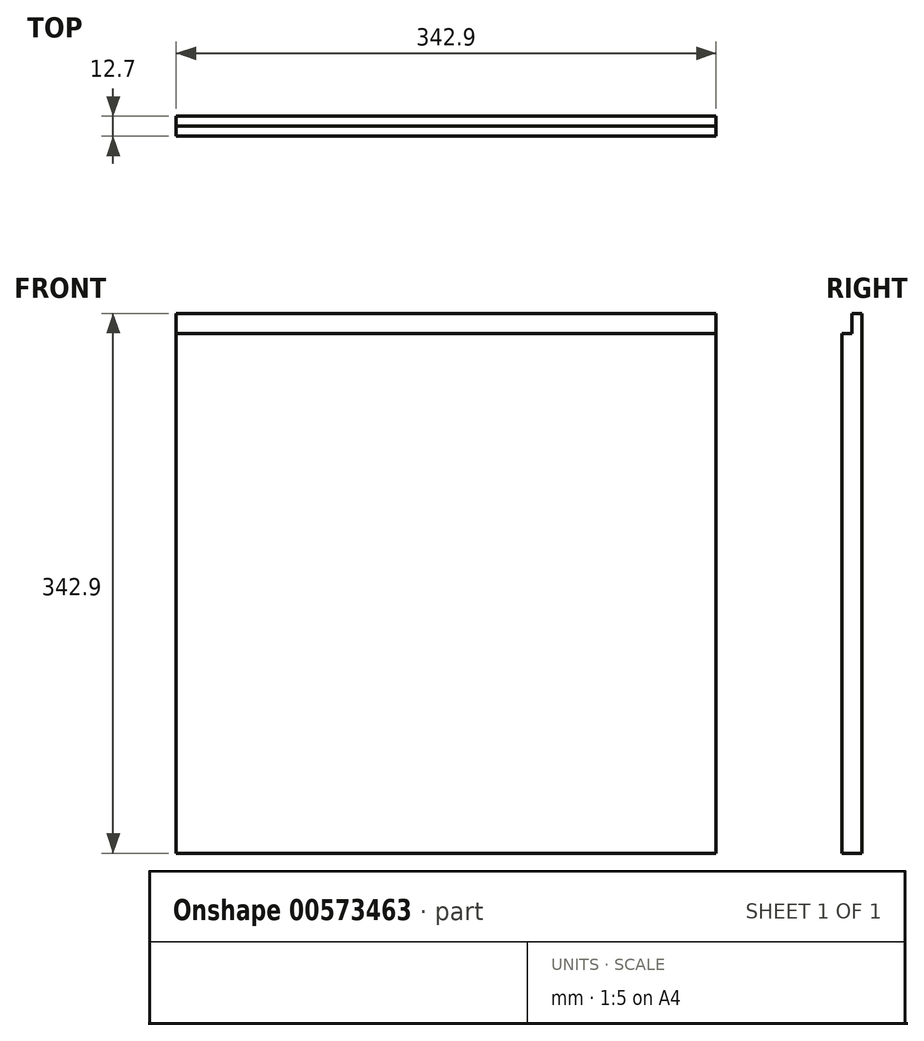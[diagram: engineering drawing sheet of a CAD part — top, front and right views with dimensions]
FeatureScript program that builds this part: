
annotation { "Feature Type Name" : "Feature", "Feature Type Description" : "" }
export const myFeature = defineFeature(function(context is Context, id is Id, definition is map)
    precondition{}
    {
        {
            var Q0;
            Q0=qCreatedBy(makeId("Front.planeOp"),FACE);
            var sketch = newSketch(context, id + "F0", { "sketchPlane" : qUnion([Q0])});
            skLineSegment(sketch, "E0.bottom", {"start": v(171.45, 171.45) * mm, "end": v(-171.45, 171.45) * mm});
            skLineSegment(sketch, "E0.top", {"start": v(171.45, -171.45) * mm, "end": v(-171.45, -171.45) * mm});
            skLineSegment(sketch, "E0.left", {"start": v(171.45, 171.45) * mm, "end": v(171.45, -171.45) * mm});
            skLineSegment(sketch, "E0.right", {"start": v(-171.45, 171.45) * mm, "end": v(-171.45, -171.45) * mm});
            skPoint(sketch, "E0.middle", {"position": v(0, 0) * mm});
            skSolve(sketch);
        }
        {
            var Q0;
            Q0 = qSketchRegion(id + "F0", true);
            extrude(context, id + "F1", {"entities" : qUnion([Q0]), "depth" : 12.7 * mm, "offsetDistance" : 25.4 * mm});
        }
        {
            var Q0;
            Q0=makeQuery(id+"F1.opExtrude","SWEPT_FACE",FACE,{"disambiguationData":[OSD([sQuery(id+"F0.wireOp",EDGE,"E0.bottom")])]});
            var sketch = newSketch(context, id + "F2", { "sketchPlane" : qUnion([Q0])});
            skLineSegment(sketch, "E1.bottom", {"start": v(-171.45, 0) * mm, "end": v(171.45, 0) * mm});
            skLineSegment(sketch, "E1.top", {"start": v(-171.45, -6.35) * mm, "end": v(171.45, -6.35) * mm});
            skLineSegment(sketch, "E1.left", {"start": v(-171.45, 0) * mm, "end": v(-171.45, -6.35) * mm});
            skLineSegment(sketch, "E1.right", {"start": v(171.45, 0) * mm, "end": v(171.45, -6.35) * mm});
            skSolve(sketch);
        }
        {
            var Q0;
            {var subQ0=sQuery(id+"F2.wireOp",EDGE,"E1.top");Q0=makeQuery(id+"F2.imprint","IMPRINT",FACE,{"disambiguationData":[TD([[makeQuery(id+"F2.imprint","IMPRINT",EDGE,{"derivedFrom":subQ0}),-1.0]])]});}
            extrude(context, id + "F3", {"entities" : qUnion([Q0]), "operationType" : NewBodyOperationType.REMOVE, "oppositeDirection" : true, "depth" : 12.7 * mm, "offsetDistance" : 25.4 * mm});
        }
    });
